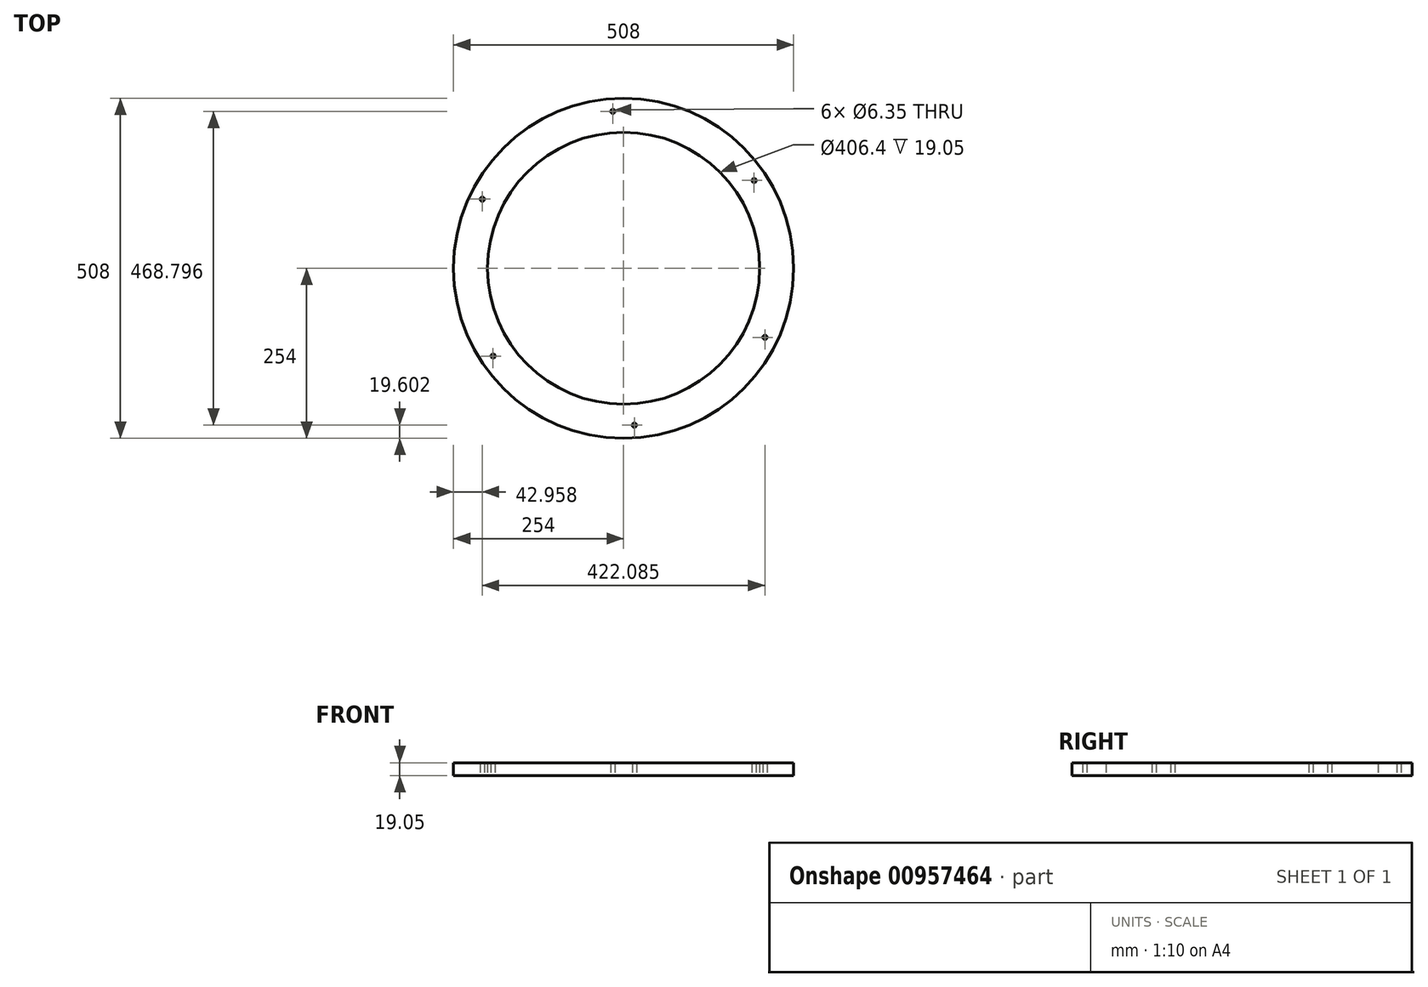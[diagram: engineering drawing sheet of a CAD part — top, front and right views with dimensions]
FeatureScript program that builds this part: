
annotation { "Feature Type Name" : "Feature", "Feature Type Description" : "" }
export const myFeature = defineFeature(function(context is Context, id is Id, definition is map)
    precondition{}
    {
        {
            var Q0;
            Q0=qCreatedBy(makeId("Top.planeOp"),FACE);
            var sketch = newSketch(context, id + "F0", { "sketchPlane" : qUnion([Q0])});
            skCircle(sketch, "E0", {"center": v(0, 0) * mm, "radius": 254 * mm});
            skCircle(sketch, "E1", {"center": v(0, 0) * mm, "radius": 234.95 * mm});
            skCircle(sketch, "E2", {"center": v(-211.04, 103.26) * mm, "radius": 3.18 * mm});
            skCircle(sketch, "E3.1.0", {"center": v(-194.95, -131.14) * mm, "radius": 3.18 * mm});
            skCircle(sketch, "E3.2.0", {"center": v(16.1, -234.4) * mm, "radius": 3.18 * mm});
            skCircle(sketch, "E4.1.3.0", {"center": v(211.04, -103.26) * mm, "radius": 3.18 * mm});
            skCircle(sketch, "E4.1.4.0", {"center": v(194.95, 131.14) * mm, "radius": 3.18 * mm});
            skCircle(sketch, "E4.1.5.0", {"center": v(-16.1, 234.4) * mm, "radius": 3.18 * mm});
            skCircle(sketch, "E5", {"center": v(0, 0) * mm, "radius": 203.2 * mm});
            skSolve(sketch);
        }
        {
            var Q0;
            {var subQ0=sQuery(id+"F0.wireOp",EDGE,"E1");var subQ1=sQuery(id+"F0.wireOp",EDGE,"E2");var subQ5=makeQuery(id+"F0.imprint","INTERSECT",VERTEX,{"disambiguationData":[OD(0.0)],"derivedFrom":[subQ1,subQ0]});Q0=makeQuery(id+"F0.imprint","IMPRINT",FACE,{"disambiguationData":[TD([[makeQuery(id+"F0.imprint","IMPRINT",EDGE,{"disambiguationData":[TD([[subQ5,1.0]])],"derivedFrom":subQ1}),-1.0]])]});}
            var Q1;
            Q1=makeQuery(id+"F0.imprint","IMPRINT",FACE,{"disambiguationData":[TD([[makeQuery(id+"F0.imprint","IMPRINT",EDGE,{"derivedFrom":sQuery(id+"F0.wireOp",EDGE,"E0")}),1.0]])]});
            extrude(context, id + "F1", {"entities" : qUnion([Q0, Q1]), "depth" : 19.05 * mm, "offsetDistance" : 25.4 * mm});
        }
    });
